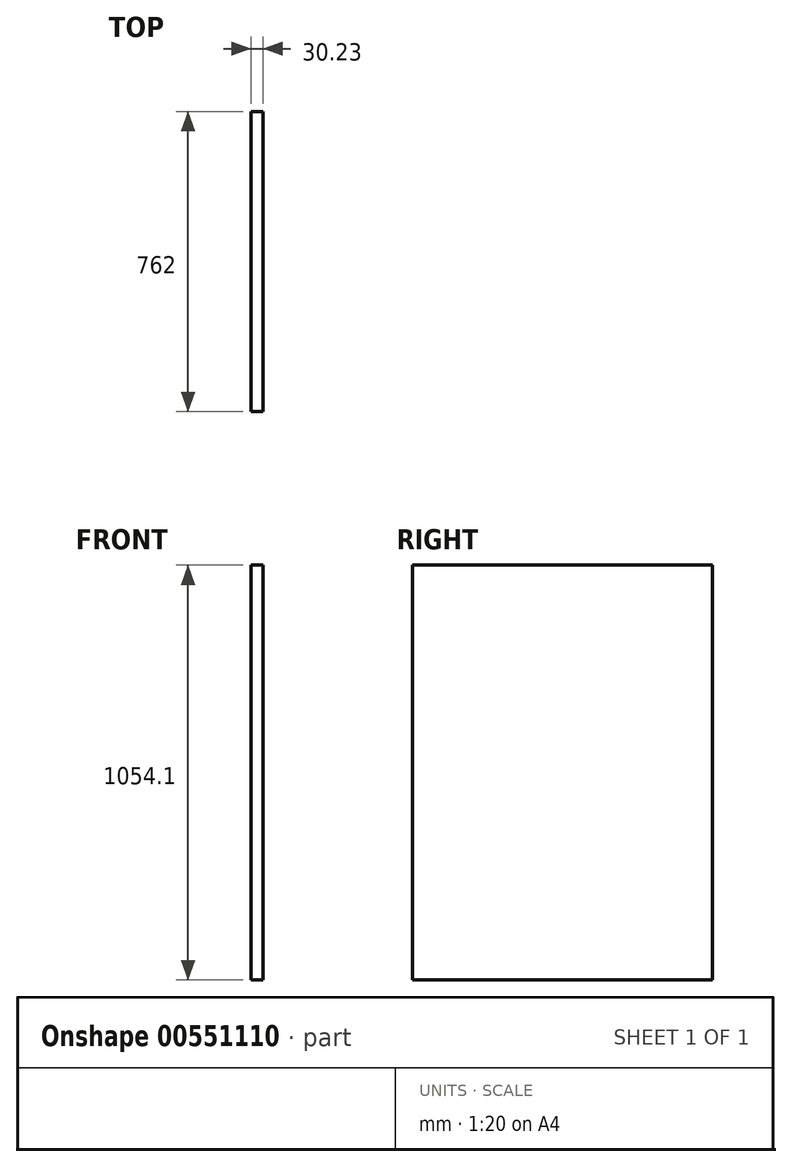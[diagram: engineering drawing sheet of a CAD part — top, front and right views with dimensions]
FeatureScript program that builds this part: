
annotation { "Feature Type Name" : "Feature", "Feature Type Description" : "" }
export const myFeature = defineFeature(function(context is Context, id is Id, definition is map)
    precondition{}
    {
        {
            var Q0;
            Q0=qCreatedBy(makeId("Right.planeOp"),FACE);
            var sketch = newSketch(context, id + "F0", { "sketchPlane" : qUnion([Q0])});
            skLineSegment(sketch, "E0.bottom", {"start": v(381, 365.13) * mm, "end": v(-381, 365.12) * mm});
            skLineSegment(sketch, "E0.top", {"start": v(381, -365.12) * mm, "end": v(-381, -365.12) * mm});
            skLineSegment(sketch, "E0.left", {"start": v(381, 365.12) * mm, "end": v(381, -365.12) * mm});
            skLineSegment(sketch, "E0.right", {"start": v(-381, 365.12) * mm, "end": v(-381, -365.12) * mm});
            skPoint(sketch, "E0.middle", {"position": v(0, 0) * mm});
            skSolve(sketch);
        }
        {
            var Q0;
            Q0=makeQuery(id+"F0.imprint","IMPRINT",FACE,{"disambiguationData":[TD([[makeQuery(id+"F0.imprint","IMPRINT",EDGE,{"derivedFrom":sQuery(id+"F0.wireOp",EDGE,"E0.bottom")}),1.0]])]});
            extrude(context, id + "F1", {"entities" : qUnion([Q0]), "depth" : 30.23 * mm, "offsetDistance" : 25.4 * mm});
        }
        {
            var Q0;
            Q0=makeQuery(id+"F1.opExtrude","SWEPT_FACE",FACE,{"disambiguationData":[OSD([sQuery(id+"F0.wireOp",EDGE,"E0.top")])]});
            extrude(context, id + "F2", {"entities" : qUnion([Q0]), "operationType" : NewBodyOperationType.ADD, "depth" : 323.85 * mm, "offsetDistance" : 25.4 * mm});
        }
    });
